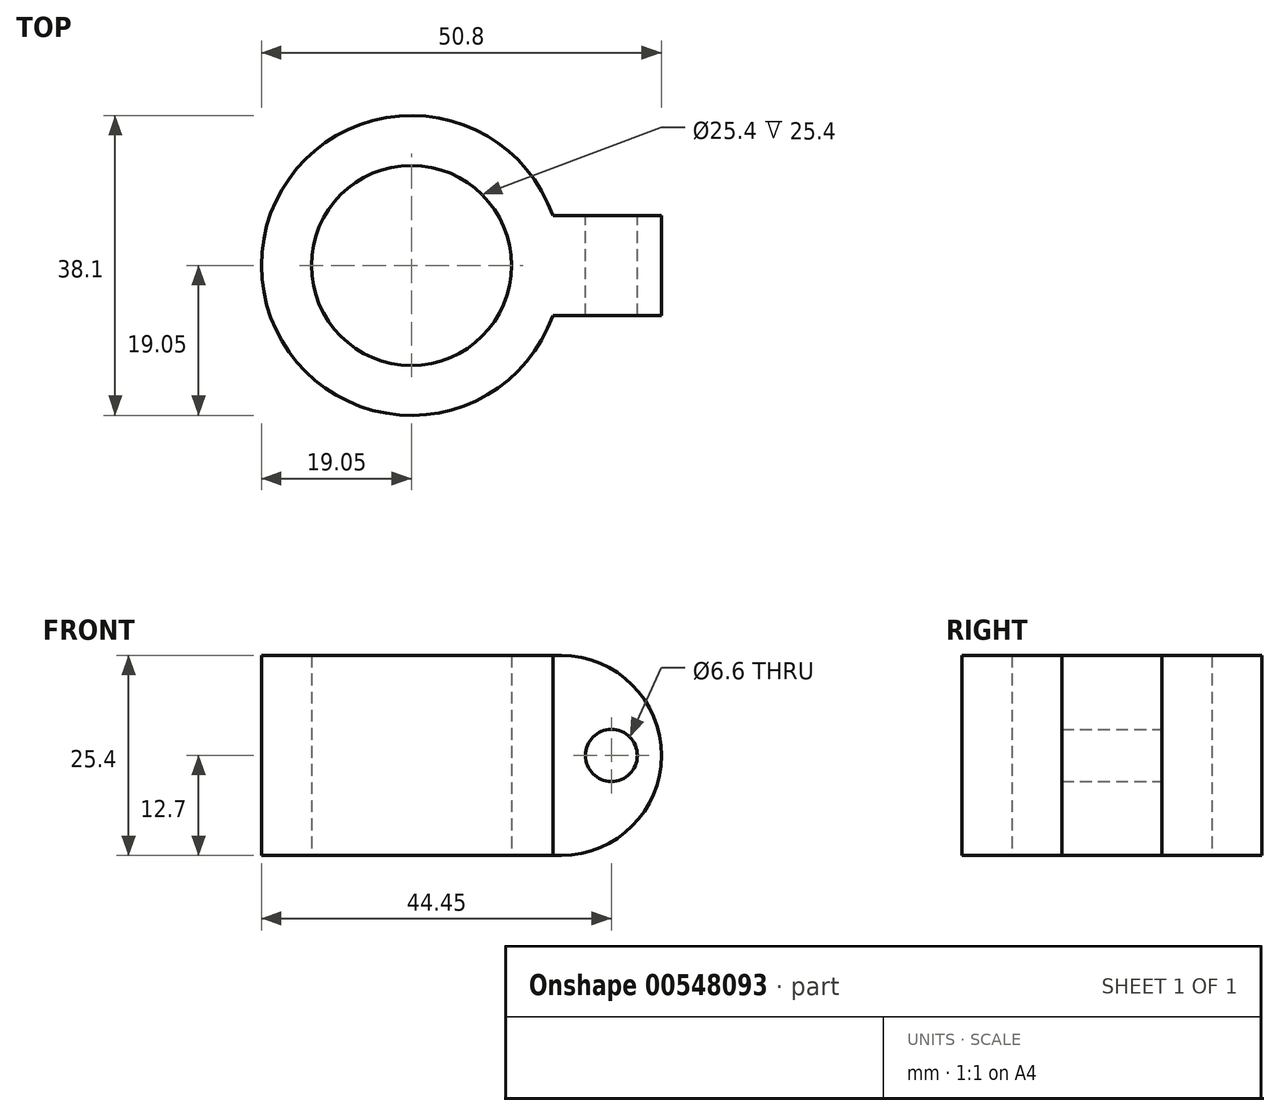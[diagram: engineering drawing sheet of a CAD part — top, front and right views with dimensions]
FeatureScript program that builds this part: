
annotation { "Feature Type Name" : "Feature", "Feature Type Description" : "" }
export const myFeature = defineFeature(function(context is Context, id is Id, definition is map)
    precondition{}
    {
        {
            var Q0;
            Q0=qCreatedBy(makeId("Front.planeOp"),FACE);
            var sketch = newSketch(context, id + "F0", { "sketchPlane" : qUnion([Q0])});
            skLineSegment(sketch, "E0.bottom", {"start": v(-12.7, 0) * mm, "end": v(-19.05, 0) * mm});
            skLineSegment(sketch, "E0.top", {"start": v(-12.7, 25.4) * mm, "end": v(-19.05, 25.4) * mm});
            skLineSegment(sketch, "E0.left", {"start": v(-12.7, 0) * mm, "end": v(-12.7, 25.4) * mm});
            skLineSegment(sketch, "E0.right", {"start": v(-19.05, 0) * mm, "end": v(-19.05, 25.4) * mm});
            skSolve(sketch);
        }
        {
            var Q0;
            Q0=qCreatedBy(makeId("Front.planeOp"),FACE);
            var sketch = newSketch(context, id + "F1", { "sketchPlane" : qUnion([Q0])});
            skLineSegment(sketch, "E1", {"start": v(0, -20.83) * mm, "end": v(0, 68.83) * mm});
            skSolve(sketch);
        }
        {
            var Q0;
            Q0=makeQuery(id+"F0.imprint","IMPRINT",FACE,{"disambiguationData":[TD([[makeQuery(id+"F0.imprint","IMPRINT",EDGE,{"derivedFrom":sQuery(id+"F0.wireOp",EDGE,"E0.bottom")}),-1.0]])]});
            var Q1;
            Q1=sQuery(id+"F1.wireOp",EDGE,"E1");
            revolve(context, id + "F2", {"entities" : qUnion([Q0]), "axis" : qUnion([Q1]), "revolveType" : RevolveType.FULL});
        }
        {
            var Q0;
            Q0=qCreatedBy(makeId("Front.planeOp"),FACE);
            var sketch = newSketch(context, id + "F3", { "sketchPlane" : qUnion([Q0])});
            skLineSegment(sketch, "E2.bottom", {"start": v(19.05, 25.4) * mm, "end": v(12.7, 25.4) * mm});
            skLineSegment(sketch, "E2.top", {"start": v(19.05, 0) * mm, "end": v(12.7, 0) * mm});
            skLineSegment(sketch, "E2.left", {"start": v(19.05, 25.4) * mm, "end": v(19.05, 0) * mm});
            skLineSegment(sketch, "E2.right", {"start": v(12.7, 25.4) * mm, "end": v(12.7, 0) * mm});
            skArc(sketch, "E3", {"start": v(19.05, 0) * mm, "mid": v(31.75, 12.7) * mm, "end": v(19.05, 25.4) * mm});
            skCircle(sketch, "E4", {"center": v(25.4, 12.7) * mm, "radius": 3.3 * mm});
            skSolve(sketch);
        }
        {
            var Q0;
            Q0 = qSketchRegion(id + "F3", true);
            extrude(context, id + "F4", {"entities" : qUnion([Q0]), "operationType" : NewBodyOperationType.ADD, "depth" : 6.35 * mm, "offsetDistance" : 25.4 * mm, "hasSecondDirection" : true, "secondDirectionOppositeDirection" : true, "secondDirectionDepth" : 6.35 * mm});
        }
    });
